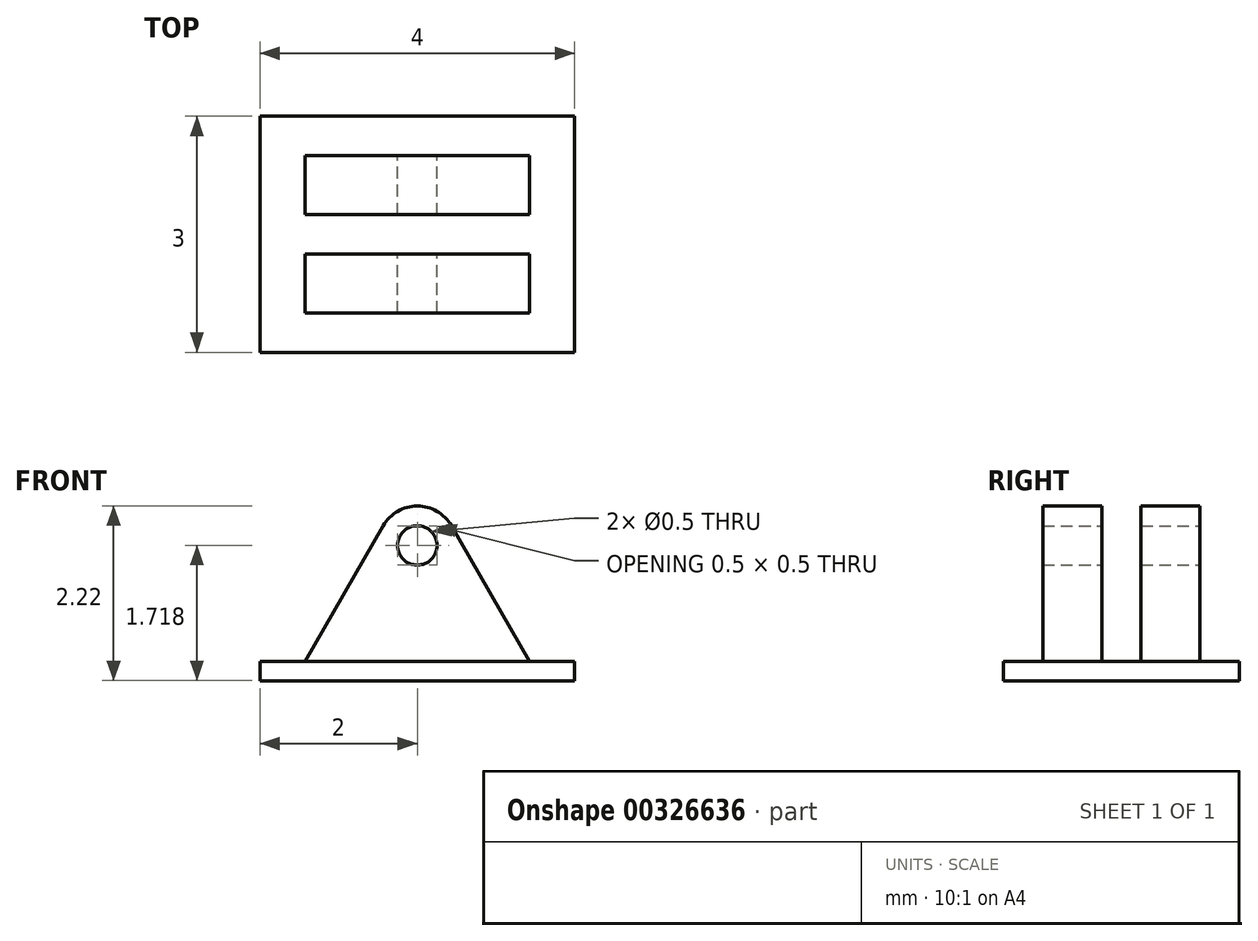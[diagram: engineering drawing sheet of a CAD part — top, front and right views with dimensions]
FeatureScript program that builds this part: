
annotation { "Feature Type Name" : "Feature", "Feature Type Description" : "" }
export const myFeature = defineFeature(function(context is Context, id is Id, definition is map)
    precondition{}
    {
        {
            var Q0;
            Q0=qCreatedBy(makeId("Front.planeOp"),FACE);
            var sketch = newSketch(context, id + "F0", { "sketchPlane" : qUnion([Q0])});
            skLineSegment(sketch, "E0", {"start": v(-1.5, 0) * mm, "end": v(-0.43, 1.85) * mm});
            skLineSegment(sketch, "E1.MirrorCS", {"start": v(1.5, 0) * mm, "end": v(0.43, 1.85) * mm});
            skArc(sketch, "E2", {"start": v(0.43, 1.85) * mm, "mid": v(0, 2.1) * mm, "end": v(-0.43, 1.85) * mm});
            skCircle(sketch, "E3", {"center": v(0, 1.6) * mm, "radius": 0.25 * mm});
            skPoint(sketch, "E4.orphan", {"position": v(0, 2.6) * mm});
            skLineSegment(sketch, "E5", {"start": v(-1.5, 0) * mm, "end": v(1.5, 0) * mm});
            skSolve(sketch);
        }
        {
            var Q0;
            Q0=makeQuery(id+"F0.imprint","IMPRINT",FACE,{"disambiguationData":[TD([[makeQuery(id+"F0.imprint","IMPRINT",EDGE,{"derivedFrom":sQuery(id+"F0.wireOp",EDGE,"E0")}),-1.0]])]});
            extrude(context, id + "F1", {"entities" : qUnion([Q0]), "endBound" : BoundingType.SYMMETRIC, "depth" : 2 * mm});
        }
        {
            var Q0;
            Q0=qCreatedBy(makeId("Top.planeOp"),FACE);
            var sketch = newSketch(context, id + "F2", { "sketchPlane" : qUnion([Q0])});
            skLineSegment(sketch, "E6.bottom", {"start": v(2.06, 0.25) * mm, "end": v(-2.06, 0.25) * mm});
            skLineSegment(sketch, "E6.top", {"start": v(2.06, -0.25) * mm, "end": v(-2.06, -0.25) * mm});
            skLineSegment(sketch, "E6.left", {"start": v(2.06, 0.25) * mm, "end": v(2.06, -0.25) * mm});
            skLineSegment(sketch, "E6.right", {"start": v(-2.06, 0.25) * mm, "end": v(-2.06, -0.25) * mm});
            skPoint(sketch, "E6.middle", {"position": v(0, 0) * mm});
            skSolve(sketch);
        }
        {
            var Q0;
            Q0=makeQuery(id+"F2.imprint","IMPRINT",FACE,{"disambiguationData":[TD([[makeQuery(id+"F2.imprint","IMPRINT",EDGE,{"derivedFrom":sQuery(id+"F2.wireOp",EDGE,"E6.bottom")}),1.0]])]});
            extrude(context, id + "F3", {"entities" : qUnion([Q0]), "operationType" : NewBodyOperationType.REMOVE, "endBound" : BoundingType.SYMMETRIC, "oppositeDirection" : true, "depth" : 25 * mm});
        }
        {
            var Q0;
            Q0=qCreatedBy(makeId("Top.planeOp"),FACE);
            var sketch = newSketch(context, id + "F4", { "sketchPlane" : qUnion([Q0])});
            skLineSegment(sketch, "E7.bottom", {"start": v(2, 1.5) * mm, "end": v(-2, 1.5) * mm});
            skLineSegment(sketch, "E7.top", {"start": v(2, -1.5) * mm, "end": v(-2, -1.5) * mm});
            skLineSegment(sketch, "E7.left", {"start": v(2, 1.5) * mm, "end": v(2, -1.5) * mm});
            skLineSegment(sketch, "E7.right", {"start": v(-2, 1.5) * mm, "end": v(-2, -1.5) * mm});
            skPoint(sketch, "E7.middle", {"position": v(0, 0) * mm});
            skSolve(sketch);
        }
        {
            var Q0;
            Q0=makeQuery(id+"F4.imprint","IMPRINT",FACE,{"disambiguationData":[TD([[makeQuery(id+"F4.imprint","IMPRINT",EDGE,{"derivedFrom":sQuery(id+"F4.wireOp",EDGE,"E7.bottom")}),1.0]])]});
            extrude(context, id + "F5", {"entities" : qUnion([Q0]), "operationType" : NewBodyOperationType.ADD, "endBound" : BoundingType.SYMMETRIC, "depth" : .25 * mm});
        }
    });
